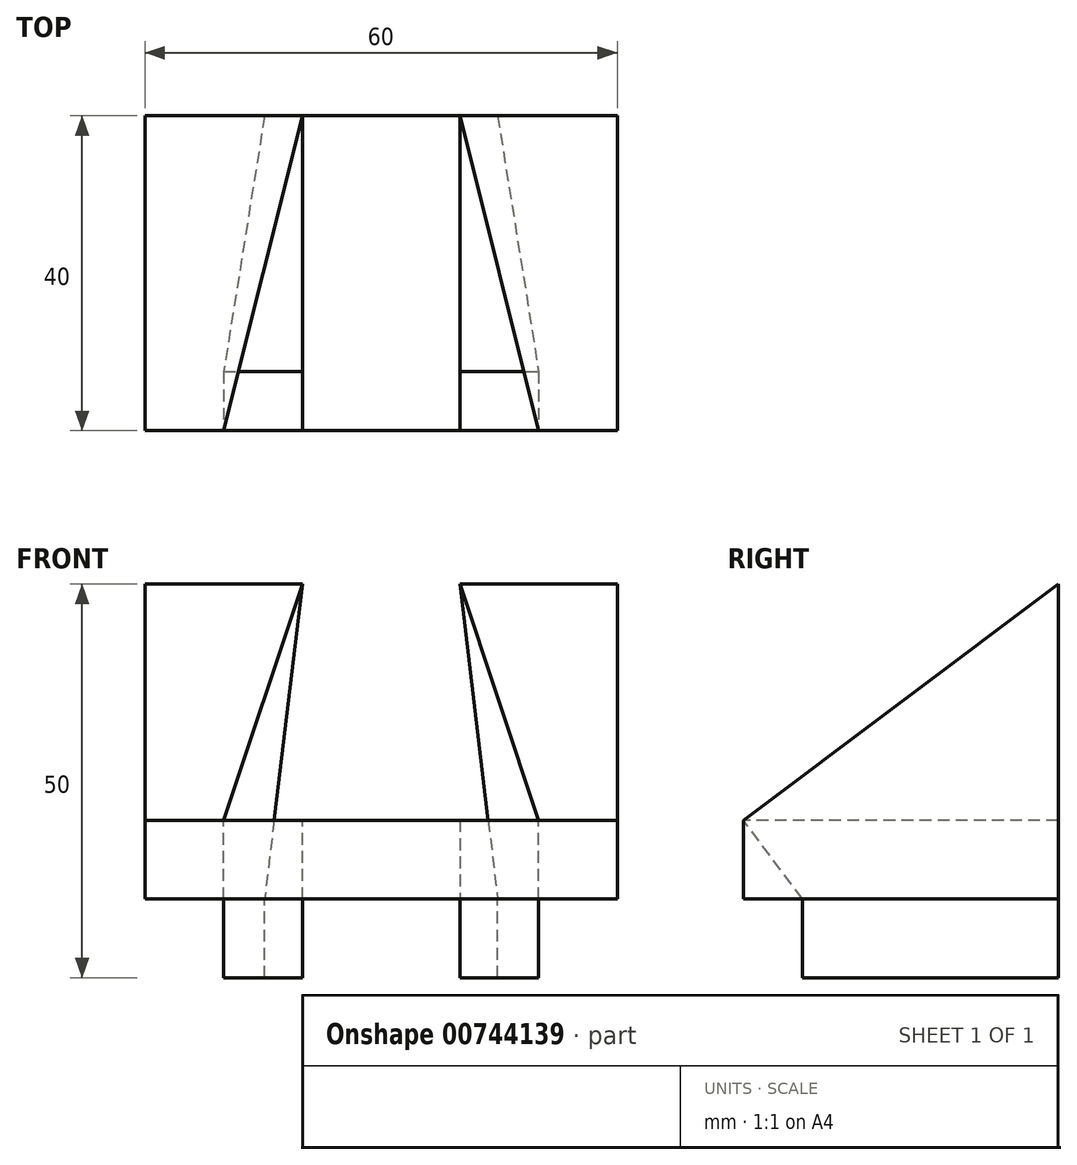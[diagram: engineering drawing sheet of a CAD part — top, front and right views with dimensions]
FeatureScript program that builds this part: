
annotation { "Feature Type Name" : "Feature", "Feature Type Description" : "" }
export const myFeature = defineFeature(function(context is Context, id is Id, definition is map)
    precondition{}
    {
        {
            var Q0;
            Q0=qCreatedBy(makeId("Front.planeOp"),FACE);
            var sketch = newSketch(context, id + "F0", { "sketchPlane" : qUnion([Q0])});
            skLineSegment(sketch, "E0", {"start": v(0, 0) * mm, "end": v(60, 0) * mm});
            skLineSegment(sketch, "E1", {"start": v(60, 0) * mm, "end": v(60, 40) * mm});
            skLineSegment(sketch, "E2", {"start": v(60, 40) * mm, "end": v(0, 40) * mm});
            skLineSegment(sketch, "E3", {"start": v(0, 40) * mm, "end": v(0, 0) * mm});
            skSolve(sketch);
        }
        {
            var Q0;
            Q0 = qSketchRegion(id + "F0", true);
            extrude(context, id + "F1", {"entities" : qUnion([Q0]), "depth" : 40 * mm, "offsetDistance" : 25 * mm});
        }
        {
            var Q0;
            Q0=makeQuery(id+"F1.opExtrude","CAP_FACE",FACE,{"disambiguationData":[OSD([sQuery(id+"F0.wireOp",EDGE,"E0"),sQuery(id+"F0.wireOp",EDGE,"E1"),sQuery(id+"F0.wireOp",EDGE,"E2"),sQuery(id+"F0.wireOp",EDGE,"E3")])],"isStart":false});
            var sketch = newSketch(context, id + "F2", { "sketchPlane" : qUnion([Q0])});
            skLineSegment(sketch, "E4", {"start": v(0, 0) * mm, "end": v(20, 0) * mm});
            skLineSegment(sketch, "E5", {"start": v(20, 0) * mm, "end": v(20, 40) * mm});
            skLineSegment(sketch, "E6", {"start": v(20, 40) * mm, "end": v(40, 40) * mm});
            skLineSegment(sketch, "E7", {"start": v(40, 40) * mm, "end": v(40, 10) * mm});
            skLineSegment(sketch, "E8", {"start": v(40, 10) * mm, "end": v(20, 10) * mm});
            skLineSegment(sketch, "E9", {"start": v(20, 10) * mm, "end": v(20, 40) * mm});
            skSolve(sketch);
        }
        {
            var Q0;
            Q0 = qSketchRegion(id + "F2", true);
            extrude(context, id + "F3", {"entities" : qUnion([Q0]), "operationType" : NewBodyOperationType.REMOVE, "oppositeDirection" : true, "depth" : 40 * mm, "offsetDistance" : 25 * mm});
        }
        {
            var Q0;
            Q0=makeQuery(id+"F1.opExtrude","SWEPT_FACE",FACE,{"disambiguationData":[OSD([sQuery(id+"F0.wireOp",EDGE,"E1")])]});
            var sketch = newSketch(context, id + "F4", { "sketchPlane" : qUnion([Q0])});
            skLineSegment(sketch, "E10", {"start": v(-40, 0) * mm, "end": v(-40, 10) * mm});
            skLineSegment(sketch, "E11", {"start": v(-40, 10) * mm, "end": v(0, 40) * mm});
            skLineSegment(sketch, "E12", {"start": v(0, 40) * mm, "end": v(-40, 40) * mm});
            skLineSegment(sketch, "E13", {"start": v(-40, 40) * mm, "end": v(-40, 10) * mm});
            skSolve(sketch);
        }
        {
            var Q0;
            Q0 = qSketchRegion(id + "F4", true);
            extrude(context, id + "F5", {"entities" : qUnion([Q0]), "operationType" : NewBodyOperationType.REMOVE, "oppositeDirection" : true, "depth" : 60 * mm, "offsetDistance" : 25 * mm});
        }
        {
            var Q0;
            {var subQ0=sQuery(id+"F0.wireOp",EDGE,"E3");Q0=makeQuery(id+"F5.boolean.opBoolean","COPY",FACE,{"disambiguationData":[TD([makeQuery(id+"F1.opExtrude","SWEPT_FACE",FACE,{"disambiguationData":[OSD([subQ0])]})])],"derivedFrom":makeQuery(id+"F5.opExtrude","SWEPT_FACE",FACE,{"disambiguationData":[OSD([sQuery(id+"F4.wireOp",EDGE,"E11")])]})});}
            var sketch = newSketch(context, id + "F6", { "sketchPlane" : qUnion([Q0])});
            skLineSegment(sketch, "E14", {"start": v(20, 24) * mm, "end": v(10, -26) * mm});
            skLineSegment(sketch, "E15", {"start": v(10, -26) * mm, "end": v(0, -26) * mm});
            skLineSegment(sketch, "E16", {"start": v(0, -26) * mm, "end": v(0, 24) * mm});
            skLineSegment(sketch, "E17", {"start": v(0, 24) * mm, "end": v(20, 24) * mm});
            skSolve(sketch);
        }
        {
            var Q0;
            {var subQ0=sQuery(id+"F0.wireOp",EDGE,"E1");Q0=makeQuery(id+"F5.boolean.opBoolean","COPY",FACE,{"disambiguationData":[TD([makeQuery(id+"F1.opExtrude","SWEPT_FACE",FACE,{"disambiguationData":[OSD([subQ0])]})])],"derivedFrom":makeQuery(id+"F5.opExtrude","SWEPT_FACE",FACE,{"disambiguationData":[OSD([sQuery(id+"F4.wireOp",EDGE,"E11")])]})});}
            var sketch = newSketch(context, id + "F7", { "sketchPlane" : qUnion([Q0])});
            skLineSegment(sketch, "E18", {"start": v(40, 24) * mm, "end": v(50, -26) * mm});
            skLineSegment(sketch, "E19", {"start": v(50, -26) * mm, "end": v(60, -26) * mm});
            skLineSegment(sketch, "E20", {"start": v(60, -26) * mm, "end": v(60, 24) * mm});
            skLineSegment(sketch, "E21", {"start": v(60, 24) * mm, "end": v(40, 24) * mm});
            skSolve(sketch);
        }
        {
            var Q0;
            {var subQ0=sQuery(id+"F6.wireOp",EDGE,"E14");Q0=makeQuery(id+"F6.imprint","IMPRINT",FACE,{"disambiguationData":[TD([[makeQuery(id+"F6.imprint","IMPRINT",EDGE,{"derivedFrom":subQ0}),1.0]])]});}
            var Q1;
            {var subQ0=sQuery(id+"F7.wireOp",EDGE,"E18");Q1=makeQuery(id+"F7.imprint","IMPRINT",FACE,{"disambiguationData":[TD([[makeQuery(id+"F7.imprint","IMPRINT",EDGE,{"derivedFrom":subQ0}),-1.0]])]});}
            extrude(context, id + "F8", {"entities" : qUnion([Q0, Q1]), "operationType" : NewBodyOperationType.REMOVE, "oppositeDirection" : true, "depth" : 40 * mm, "offsetDistance" : 25 * mm});
        }
        {
            var Q0;
            Q0=makeQuery(id+"F1.opExtrude","SWEPT_FACE",FACE,{"disambiguationData":[OSD([sQuery(id+"F0.wireOp",EDGE,"E0")])]});
            var sketch = newSketch(context, id + "F9", { "sketchPlane" : qUnion([Q0])});
            skLineSegment(sketch, "E22", {"start": v(20, 0) * mm, "end": v(20, 32.5) * mm});
            skLineSegment(sketch, "E23", {"start": v(20, 32.5) * mm, "end": v(10, 32.5) * mm});
            skLineSegment(sketch, "E24", {"start": v(10, 32.5) * mm, "end": v(15.2, 0) * mm});
            skLineSegment(sketch, "E25", {"start": v(15.2, 0) * mm, "end": v(40, 0) * mm});
            skLineSegment(sketch, "E26", {"start": v(40, 0) * mm, "end": v(40, 32.5) * mm});
            skLineSegment(sketch, "E27", {"start": v(40, 32.5) * mm, "end": v(50, 32.5) * mm});
            skLineSegment(sketch, "E28", {"start": v(50, 32.5) * mm, "end": v(44.8, 0) * mm});
            skLineSegment(sketch, "E29", {"start": v(44.8, 0) * mm, "end": v(40, 0) * mm});
            skSolve(sketch);
        }
        {
            var Q0;
            Q0 = qSketchRegion(id + "F9", true);
            extrude(context, id + "F10", {"entities" : qUnion([Q0]), "operationType" : NewBodyOperationType.ADD, "depth" : 10 * mm, "offsetDistance" : 25 * mm});
        }
    });
